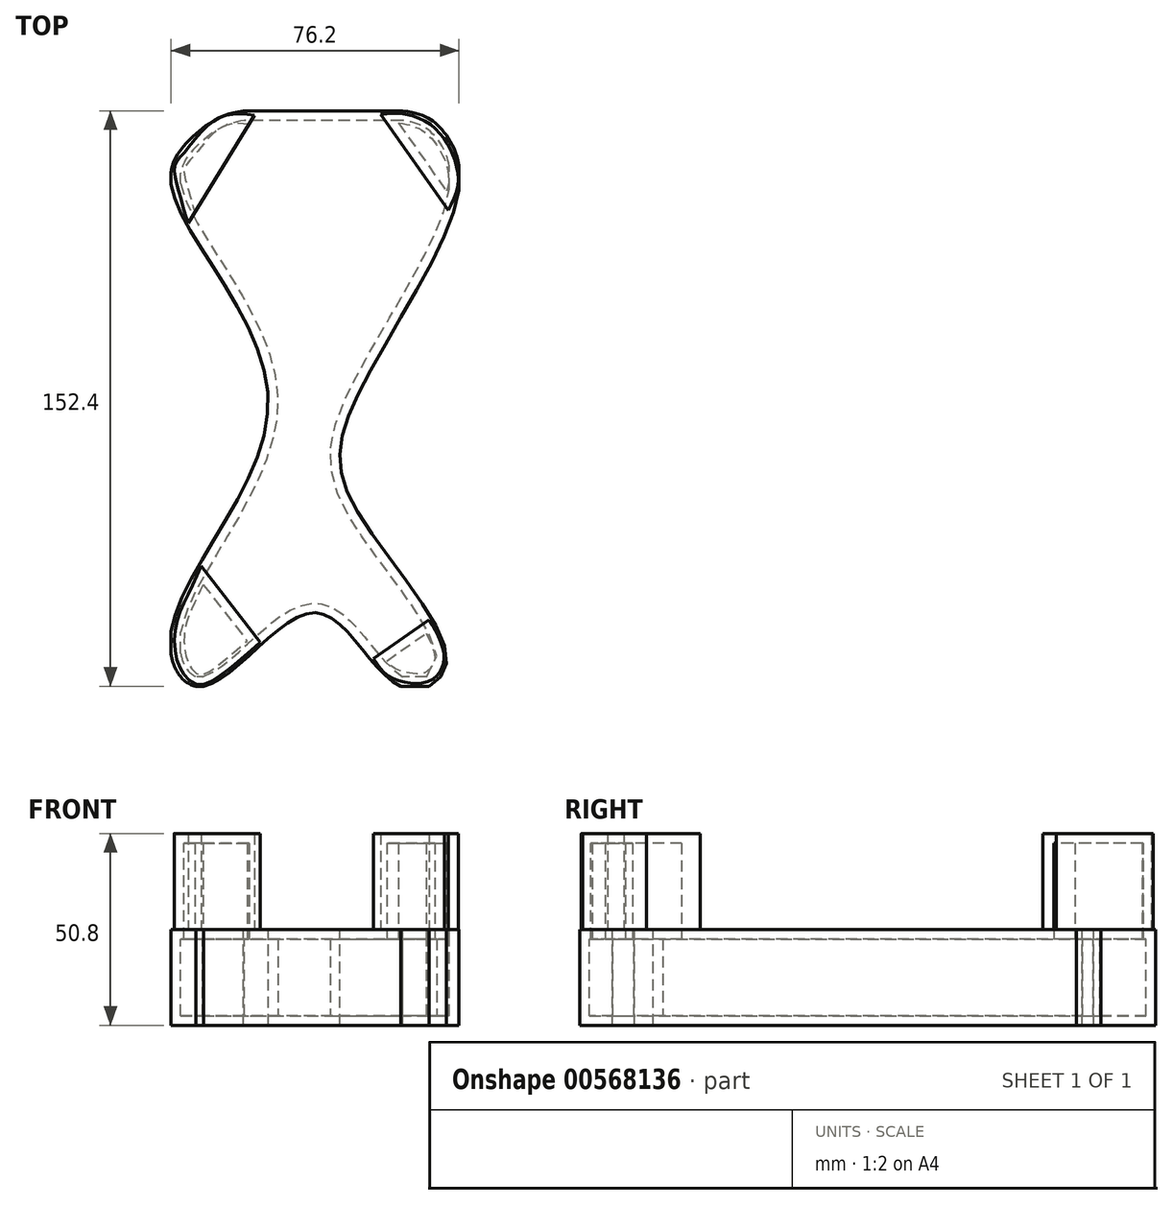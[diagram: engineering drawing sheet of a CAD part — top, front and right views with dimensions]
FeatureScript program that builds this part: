
annotation { "Feature Type Name" : "Feature", "Feature Type Description" : "" }
export const myFeature = defineFeature(function(context is Context, id is Id, definition is map)
    precondition{}
    {
        {
            var Q0;
            Q0=qCreatedBy(makeId("Top.planeOp"),FACE);
            var sketch = newSketch(context, id + "F0", { "sketchPlane" : qUnion([Q0])});
            skLineSegment(sketch, "E0.bottom", {"start": v(38.1, -76.2) * mm, "end": v(-38.1, -76.2) * mm});
            skLineSegment(sketch, "E0.top", {"start": v(38.1, 76.2) * mm, "end": v(-38.1, 76.2) * mm});
            skLineSegment(sketch, "E0.left", {"start": v(38.1, -76.2) * mm, "end": v(38.1, 76.2) * mm});
            skLineSegment(sketch, "E0.right", {"start": v(-38.1, -76.2) * mm, "end": v(-38.1, 76.2) * mm});
            skPoint(sketch, "E0.middle", {"position": v(0, 0) * mm});
            skSolve(sketch);
        }
        {
            var Q0;
            Q0 = qSketchRegion(id + "F0", true);
            extrude(context, id + "F1", {"entities" : qUnion([Q0]), "depth" : 25.4 * mm, "offsetDistance" : 25.4 * mm});
        }
        {
            var Q0;
            Q0=makeQuery(id+"F1.opExtrude","CAP_FACE",FACE,{"disambiguationData":[OSD([sQuery(id+"F0.wireOp",EDGE,"E0.bottom"),sQuery(id+"F0.wireOp",EDGE,"E0.top"),sQuery(id+"F0.wireOp",EDGE,"E0.left"),sQuery(id+"F0.wireOp",EDGE,"E0.right")])],"isStart":false});
            var sketch = newSketch(context, id + "F2", { "sketchPlane" : qUnion([Q0])});
            skFitSpline(sketch, "E1", {"points": [v(-18.92, 76.2) * mm, v(-30.4, 71.02) * mm, v(-38.1, 56.75) * mm, v(-12.4, 0) * mm, v(-38.1, -61.71) * mm, v(-29.46, -76.2) * mm, v(0, -56.75) * mm, v(22.64, -76.2) * mm, v(34.73, -70.09) * mm, v(10.54, -28.84) * mm, v(10.85, 0) * mm, v(38.1, 55.2) * mm, v(33.18, 71.64) * mm, v(23.26, 76.2) * mm, v(-18.92, 76.2) * mm]});
            skSolve(sketch);
        }
        {
            var Q0;
            {var subQ0=sQuery(id+"F2.wireOp",EDGE,"E1");var subQ1=makeQuery(id+"F1.opExtrude","CAP_EDGE",EDGE,{"disambiguationData":[OSD([sQuery(id+"F0.wireOp",EDGE,"E0.right")])],"isStart":false});var subQ2=makeQuery(id+"F2.imprint","INTERSECT",VERTEX,{"disambiguationData":[OD(1.0)],"derivedFrom":[subQ1,subQ0]});Q0=makeQuery(id+"F2.imprint","IMPRINT",FACE,{"disambiguationData":[TD([[makeQuery(id+"F2.imprint","IMPRINT",EDGE,{"disambiguationData":[TD([[subQ2,-1.0]])],"derivedFrom":subQ0}),-1.0]])]});}
            var Q1;
            {var subQ0=sQuery(id+"F2.wireOp",EDGE,"E1");var subQ1=makeQuery(id+"F1.opExtrude","CAP_EDGE",EDGE,{"disambiguationData":[OSD([sQuery(id+"F0.wireOp",EDGE,"E0.bottom")])],"isStart":false});var subQ2=makeQuery(id+"F2.imprint","INTERSECT",VERTEX,{"disambiguationData":[OD(3.0)],"derivedFrom":[subQ1,subQ0]});Q1=makeQuery(id+"F2.imprint","IMPRINT",FACE,{"disambiguationData":[TD([[makeQuery(id+"F2.imprint","IMPRINT",EDGE,{"disambiguationData":[TD([[subQ2,-1.0]])],"derivedFrom":subQ0}),-1.0]])]});}
            var Q2;
            {var subQ0=sQuery(id+"F2.wireOp",EDGE,"E1");var subQ1=makeQuery(id+"F1.opExtrude","CAP_EDGE",EDGE,{"disambiguationData":[OSD([sQuery(id+"F0.wireOp",EDGE,"E0.bottom")])],"isStart":false});var subQ2=makeQuery(id+"F2.imprint","INTERSECT",VERTEX,{"disambiguationData":[OD(1.0)],"derivedFrom":[subQ1,subQ0]});Q2=makeQuery(id+"F2.imprint","IMPRINT",FACE,{"disambiguationData":[TD([[makeQuery(id+"F2.imprint","IMPRINT",EDGE,{"disambiguationData":[TD([[subQ2,-1.0]])],"derivedFrom":subQ0}),-1.0]])]});}
            var Q3;
            {var subQ0=sQuery(id+"F2.wireOp",EDGE,"E1");var subQ1=makeQuery(id+"F1.opExtrude","CAP_EDGE",EDGE,{"disambiguationData":[OSD([sQuery(id+"F0.wireOp",EDGE,"E0.right")])],"isStart":false});var subQ2=makeQuery(id+"F2.imprint","INTERSECT",VERTEX,{"disambiguationData":[OD(3.0)],"derivedFrom":[subQ1,subQ0]});Q3=makeQuery(id+"F2.imprint","IMPRINT",FACE,{"disambiguationData":[TD([[makeQuery(id+"F2.imprint","IMPRINT",EDGE,{"disambiguationData":[TD([[subQ2,-1.0]])],"derivedFrom":subQ0}),-1.0]])]});}
            var Q4;
            {var subQ0=sQuery(id+"F2.wireOp",EDGE,"E1");var subQ1=makeQuery(id+"F1.opExtrude","CAP_EDGE",EDGE,{"disambiguationData":[OSD([sQuery(id+"F0.wireOp",EDGE,"E0.right")])],"isStart":false});var subQ2=makeQuery(id+"F2.imprint","INTERSECT",VERTEX,{"disambiguationData":[OD(0.0)],"derivedFrom":[subQ1,subQ0]});Q4=makeQuery(id+"F2.imprint","IMPRINT",FACE,{"disambiguationData":[TD([[makeQuery(id+"F2.imprint","IMPRINT",EDGE,{"disambiguationData":[TD([[subQ2,1.0]])],"derivedFrom":subQ0}),-1.0]])]});}
            var Q5;
            {var subQ0=sQuery(id+"F2.wireOp",EDGE,"E1");var subQ1=makeQuery(id+"F1.opExtrude","CAP_EDGE",EDGE,{"disambiguationData":[OSD([sQuery(id+"F0.wireOp",EDGE,"E0.left")])],"isStart":false});var subQ2=makeQuery(id+"F2.imprint","INTERSECT",VERTEX,{"disambiguationData":[OD(1.0)],"derivedFrom":[subQ1,subQ0]});Q5=makeQuery(id+"F2.imprint","IMPRINT",FACE,{"disambiguationData":[TD([[makeQuery(id+"F2.imprint","IMPRINT",EDGE,{"disambiguationData":[TD([[subQ2,-1.0]])],"derivedFrom":subQ0}),-1.0]])]});}
            extrude(context, id + "F3", {"entities" : qUnion([Q0, Q1, Q2, Q3, Q4, Q5]), "operationType" : NewBodyOperationType.REMOVE, "oppositeDirection" : true, "depth" : 50.8 * mm, "offsetDistance" : 25.4 * mm});
        }
        {
            var Q0;
            Q0=makeQuery(id+"F1.opExtrude","CAP_FACE",FACE,{"disambiguationData":[OSD([sQuery(id+"F0.wireOp",EDGE,"E0.bottom"),sQuery(id+"F0.wireOp",EDGE,"E0.top"),sQuery(id+"F0.wireOp",EDGE,"E0.left"),sQuery(id+"F0.wireOp",EDGE,"E0.right")])],"isStart":false});
            var sketch = newSketch(context, id + "F4", { "sketchPlane" : qUnion([Q0])});
            skSolve(sketch);
        }
        {
            var Q0;
            {var subQ8=sQuery(id+"F0.wireOp",EDGE,"E0.top");var subQ15=makeQuery(id+"F1.opExtrude","CAP_EDGE",EDGE,{"disambiguationData":[OSD([subQ8])],"isStart":false});Q0=makeQuery(id+"F4.imprint","IMPRINT",FACE,{"disambiguationData":[TD([[makeQuery(id+"F4.imprint","IMPRINT",EDGE,{"derivedFrom":subQ15}),1.0]])]});}
            var sketch = newSketch(context, id + "F5", { "sketchPlane" : qUnion([Q0])});
            skLineSegment(sketch, "E2", {"start": v(-30.18, -44.41) * mm, "end": v(-14.46, -64.53) * mm});
            skFitSpline(sketch, "E3", {"points": [v(-30.18, -44.41) * mm, v(-33.95, -52.58) * mm, v(-36.78, -59.81) * mm, v(-36.78, -68.3) * mm, v(-34.26, -73.64) * mm, v(-30.18, -75.84) * mm, v(-22.95, -71.76) * mm, v(-16.97, -66.73) * mm, v(-14.46, -64.53) * mm], "startDerivative": vector(-26.36, -58.1) * mm, "endDerivative": vector(25.8, 22.7) * mm});
            skLineSegment(sketch, "E4", {"start": v(15.4, -68.92) * mm, "end": v(30.18, -58.55) * mm});
            skFitSpline(sketch, "E5", {"points": [v(30.18, -58.55) * mm, v(33.32, -64.52) * mm, v(33.95, -70.5) * mm, v(30.18, -74.9) * mm, v(24.52, -75.2) * mm, v(19.18, -73.32) * mm, v(15.4, -68.92) * mm], "startDerivative": vector(19.78, -32.83) * mm, "endDerivative": vector(-20.48, 30.25) * mm});
            skLineSegment(sketch, "E6", {"start": v(-16.01, 74.98) * mm, "end": v(-33.6, 46.39) * mm});
            skFitSpline(sketch, "E7", {"points": [v(-16.01, 74.98) * mm, v(-23.55, 74.98) * mm, v(-29.83, 70.9) * mm, v(-34.23, 65.56) * mm, v(-37.06, 61.8) * mm, v(-36.43, 56.13) * mm, v(-33.6, 46.39) * mm], "startDerivative": vector(-44.7, 5.57) * mm, "endDerivative": vector(15.07, -50.86) * mm});
            skLineSegment(sketch, "E8", {"start": v(17.32, 75.3) * mm, "end": v(35.24, 49.84) * mm});
            skFitSpline(sketch, "E9", {"points": [v(17.32, 75.3) * mm, v(23.6, 75.3) * mm, v(30.2, 72.8) * mm, v(34.6, 68.08) * mm, v(37.12, 62.73) * mm, v(37.75, 56.13) * mm, v(35.24, 49.84) * mm], "startDerivative": vector(37.84, 2.86) * mm, "endDerivative": vector(-19.05, -36.02) * mm});
            skSolve(sketch);
        }
        {
            var Q0;
            Q0=makeQuery(id+"F5.imprint","IMPRINT",FACE,{"disambiguationData":[TD([[makeQuery(id+"F5.imprint","IMPRINT",EDGE,{"derivedFrom":sQuery(id+"F5.wireOp",EDGE,"E2")}),-1.0]])]});
            var Q1;
            Q1=makeQuery(id+"F5.imprint","IMPRINT",FACE,{"disambiguationData":[TD([[makeQuery(id+"F5.imprint","IMPRINT",EDGE,{"derivedFrom":sQuery(id+"F5.wireOp",EDGE,"E4")}),-1.0]])]});
            var Q2;
            Q2=makeQuery(id+"F5.imprint","IMPRINT",FACE,{"disambiguationData":[TD([[makeQuery(id+"F5.imprint","IMPRINT",EDGE,{"derivedFrom":sQuery(id+"F5.wireOp",EDGE,"E8")}),1.0]])]});
            var Q3;
            Q3=makeQuery(id+"F5.imprint","IMPRINT",FACE,{"disambiguationData":[TD([[makeQuery(id+"F5.imprint","IMPRINT",EDGE,{"derivedFrom":sQuery(id+"F5.wireOp",EDGE,"E6")}),-1.0]])]});
            extrude(context, id + "F6", {"entities" : qUnion([Q0, Q1, Q2, Q3]), "operationType" : NewBodyOperationType.ADD, "depth" : 25.4 * mm, "offsetDistance" : 25.4 * mm});
        }
        {
            var Q0;
            Q0=makeQuery(id+"F6.opExtrude","SWEPT_FACE",FACE,{"disambiguationData":[OSD([sQuery(id+"F5.wireOp",EDGE,"E6")])]});
            shell(context, id + "F7", {"entities" : qUnion([Q0]), "thickness" : 2.54 * mm});
        }
    });
